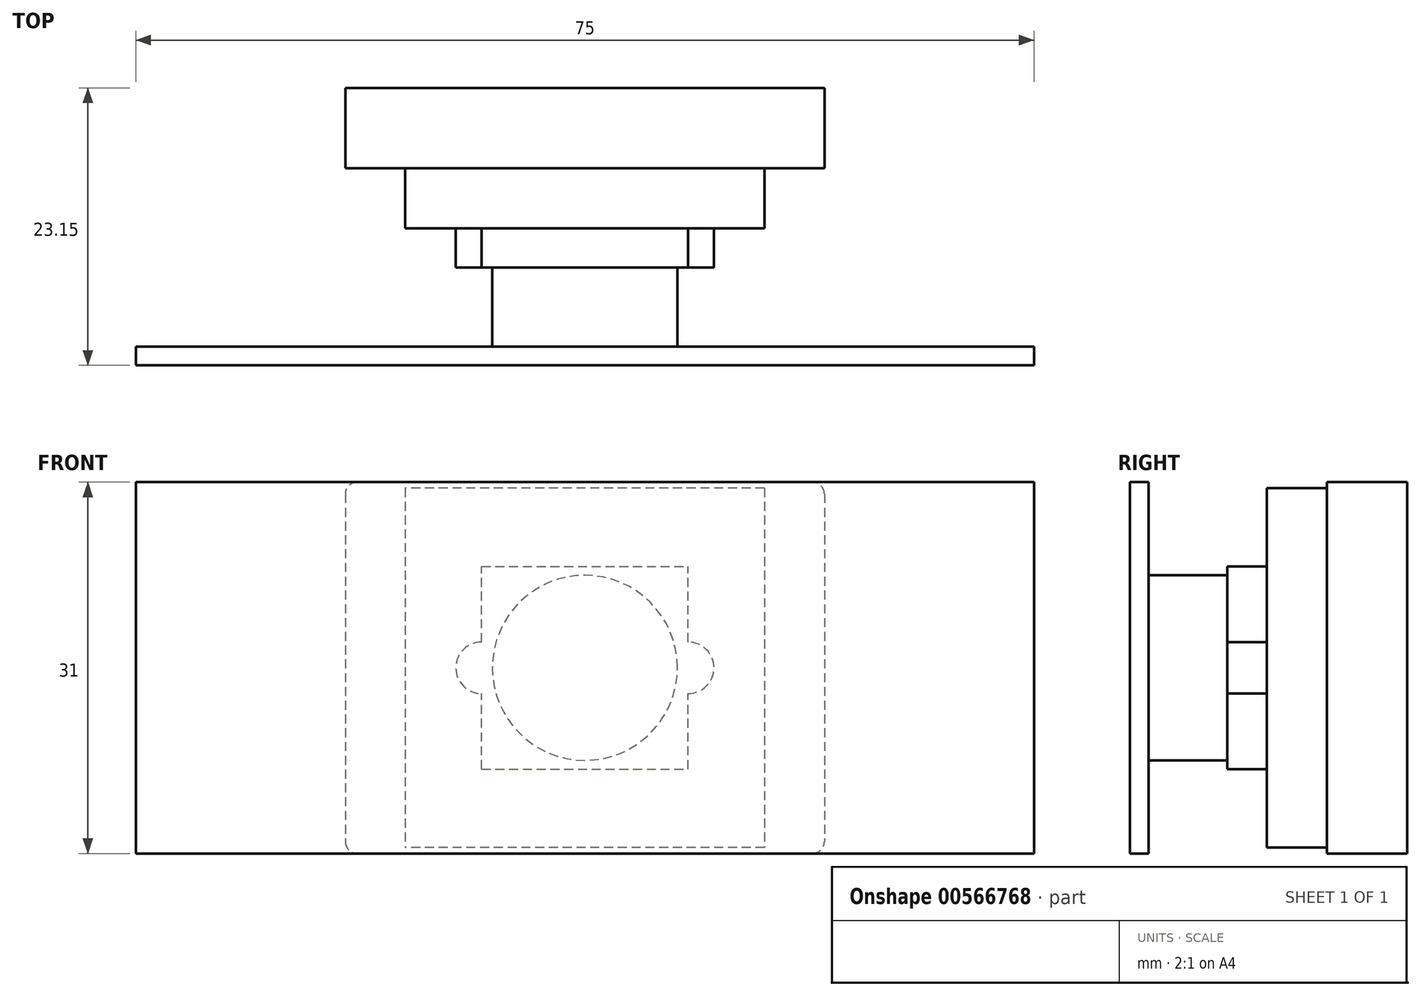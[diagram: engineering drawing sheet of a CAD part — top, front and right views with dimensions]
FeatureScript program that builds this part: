
annotation { "Feature Type Name" : "Feature", "Feature Type Description" : "" }
export const myFeature = defineFeature(function(context is Context, id is Id, definition is map)
    precondition{}
    {
        {
            var Q0;
            Q0=qCreatedBy(makeId("Front.planeOp"),FACE);
            var sketch = newSketch(context, id + "F0", { "sketchPlane" : qUnion([Q0])});
            skLineSegment(sketch, "E0.bottom", {"start": v(20, 15.5) * mm, "end": v(-20, 15.5) * mm});
            skLineSegment(sketch, "E0.top", {"start": v(20, -15.5) * mm, "end": v(-20, -15.5) * mm});
            skLineSegment(sketch, "E0.left", {"start": v(20, 15.5) * mm, "end": v(20, -15.5) * mm});
            skLineSegment(sketch, "E0.right", {"start": v(-20, 15.5) * mm, "end": v(-20, -15.5) * mm});
            skPoint(sketch, "E0.middle", {"position": v(0, 0) * mm});
            skSolve(sketch);
        }
        {
            var Q0;
            Q0=makeQuery(id+"F0.imprint","IMPRINT",FACE,{"disambiguationData":[TD([[makeQuery(id+"F0.imprint","IMPRINT",EDGE,{"derivedFrom":sQuery(id+"F0.wireOp",EDGE,"E0.bottom")}),1.0]])]});
            extrude(context, id + "F1", {"entities" : qUnion([Q0]), "oppositeDirection" : true, "depth" : 6.7 * mm, "offsetDistance" : 25.4 * mm});
        }
        {
            var Q0;
            Q0=makeQuery(id+"F1.opExtrude","SWEPT_EDGE",EDGE,{"disambiguationData":[OSD([sQuery(id+"F0.wireOp",EDGE,"E0.bottom"),sQuery(id+"F0.wireOp",EDGE,"E0.right")])]});
            var Q1;
            Q1=makeQuery(id+"F1.opExtrude","SWEPT_EDGE",EDGE,{"disambiguationData":[OSD([sQuery(id+"F0.wireOp",EDGE,"E0.top"),sQuery(id+"F0.wireOp",EDGE,"E0.right")])]});
            var Q2;
            Q2=makeQuery(id+"F1.opExtrude","SWEPT_EDGE",EDGE,{"disambiguationData":[OSD([sQuery(id+"F0.wireOp",EDGE,"E0.bottom"),sQuery(id+"F0.wireOp",EDGE,"E0.left")])]});
            var Q3;
            Q3=makeQuery(id+"F1.opExtrude","SWEPT_EDGE",EDGE,{"disambiguationData":[OSD([sQuery(id+"F0.wireOp",EDGE,"E0.top"),sQuery(id+"F0.wireOp",EDGE,"E0.left")])]});
            fillet(context, id + "F2", {"entities" : qUnion([Q0, Q1, Q2, Q3]), "radius" : 1 * mm, "tangentPropagation" : true, "allowEdgeOverflow" : false});
        }
        {
            var Q0;
            Q0=makeQuery(id+"F1.opExtrude","CAP_FACE",FACE,{"disambiguationData":[OSD([sQuery(id+"F0.wireOp",EDGE,"E0.bottom"),sQuery(id+"F0.wireOp",EDGE,"E0.top"),sQuery(id+"F0.wireOp",EDGE,"E0.left"),sQuery(id+"F0.wireOp",EDGE,"E0.right")])],"isStart":true});
            var sketch = newSketch(context, id + "F3", { "sketchPlane" : qUnion([Q0])});
            skLineSegment(sketch, "E1.bottom", {"start": v(15, 15) * mm, "end": v(-15, 15) * mm});
            skLineSegment(sketch, "E1.top", {"start": v(15, -15) * mm, "end": v(-15, -15) * mm});
            skLineSegment(sketch, "E1.left", {"start": v(15, 15) * mm, "end": v(15, -15) * mm});
            skLineSegment(sketch, "E1.right", {"start": v(-15, 15) * mm, "end": v(-15, -15) * mm});
            skPoint(sketch, "E1.middle", {"position": v(0, 0) * mm});
            skSolve(sketch);
        }
        {
            var Q0;
            Q0=makeQuery(id+"F3.imprint","IMPRINT",FACE,{"disambiguationData":[TD([[makeQuery(id+"F3.imprint","IMPRINT",EDGE,{"derivedFrom":sQuery(id+"F3.wireOp",EDGE,"E1.bottom")}),1.0]])]});
            extrude(context, id + "F4", {"entities" : qUnion([Q0]), "operationType" : NewBodyOperationType.ADD, "depth" : 5 * mm, "offsetDistance" : 25.4 * mm});
        }
        {
            var Q0;
            Q0=makeQuery(id+"F1.opExtrude","CAP_FACE",FACE,{"disambiguationData":[OSD([sQuery(id+"F0.wireOp",EDGE,"E0.bottom"),sQuery(id+"F0.wireOp",EDGE,"E0.top"),sQuery(id+"F0.wireOp",EDGE,"E0.left"),sQuery(id+"F0.wireOp",EDGE,"E0.right")])],"isStart":true});
            var sketch = newSketch(context, id + "F5", { "sketchPlane" : qUnion([Q0])});
            skLineSegment(sketch, "E2.bottom", {"start": v(8.62, 8.45) * mm, "end": v(-8.62, 8.45) * mm});
            skLineSegment(sketch, "E2.top", {"start": v(8.63, -8.45) * mm, "end": v(-8.62, -8.45) * mm});
            skLineSegment(sketch, "E2.left", {"start": v(8.62, 8.45) * mm, "end": v(8.63, -8.45) * mm});
            skLineSegment(sketch, "E2.right", {"start": v(-8.62, 8.45) * mm, "end": v(-8.62, -8.45) * mm});
            skPoint(sketch, "E2.middle", {"position": v(0, 0) * mm});
            skArc(sketch, "E3", {"start": v(-8.63, 2.15) * mm, "mid": v(-10.78, 0) * mm, "end": v(-8.63, -2.15) * mm});
            skArc(sketch, "E4", {"start": v(8.62, -2.15) * mm, "mid": v(10.78, 0) * mm, "end": v(8.62, 2.15) * mm});
            skSolve(sketch);
        }
        {
            var Q0;
            Q0 = qSketchRegion(id + "F5", true);
            extrude(context, id + "F6", {"entities" : qUnion([Q0]), "operationType" : NewBodyOperationType.ADD, "depth" : 8.3 * mm, "offsetDistance" : 25.4 * mm});
        }
        {
            var Q0;
            Q0=makeQuery(id+"F6.opExtrude","CAP_FACE",FACE,{"disambiguationData":[OSD([sQuery(id+"F5.wireOp",EDGE,"E2.bottom"),sQuery(id+"F5.wireOp",EDGE,"E2.top"),sQuery(id+"F5.wireOp",EDGE,"E2.left"),sQuery(id+"F5.wireOp",EDGE,"E2.right"),sQuery(id+"F5.wireOp",EDGE,"E3"),sQuery(id+"F5.wireOp",EDGE,"E4")])],"isStart":false});
            var sketch = newSketch(context, id + "F7", { "sketchPlane" : qUnion([Q0])});
            skCircle(sketch, "E5", {"center": v(0, 0) * mm, "radius": 7.73 * mm});
            skSolve(sketch);
        }
        {
            var Q0;
            Q0=makeQuery(id+"F7.imprint","IMPRINT",FACE,{"disambiguationData":[TD([[makeQuery(id+"F7.imprint","IMPRINT",EDGE,{"derivedFrom":sQuery(id+"F7.wireOp",EDGE,"E5")}),1.0]])]});
            extrude(context, id + "F8", {"entities" : qUnion([Q0]), "operationType" : NewBodyOperationType.ADD, "depth" : 8.15 * mm, "offsetDistance" : 25.4 * mm});
        }
        {
            var Q0;
            Q0=makeQuery(id+"F8.opExtrude","CAP_FACE",FACE,{"disambiguationData":[OSD([sQuery(id+"F7.wireOp",EDGE,"E5")])],"isStart":false});
            var sketch = newSketch(context, id + "F9", { "sketchPlane" : qUnion([Q0])});
            skLineSegment(sketch, "E6.bottom", {"start": v(37.5, 15.5) * mm, "end": v(-37.5, 15.5) * mm});
            skLineSegment(sketch, "E6.top", {"start": v(37.5, -15.5) * mm, "end": v(-37.5, -15.5) * mm});
            skLineSegment(sketch, "E6.left", {"start": v(37.5, 15.5) * mm, "end": v(37.5, -15.5) * mm});
            skLineSegment(sketch, "E6.right", {"start": v(-37.5, 15.5) * mm, "end": v(-37.5, -15.5) * mm});
            skPoint(sketch, "E6.middle", {"position": v(0, 0) * mm});
            skSolve(sketch);
        }
        {
            var Q0;
            Q0 = qSketchRegion(id + "F9", true);
            extrude(context, id + "F10", {"entities" : qUnion([Q0]), "operationType" : NewBodyOperationType.ADD, "oppositeDirection" : true, "depth" : 1.57 * mm, "offsetDistance" : 25.4 * mm});
        }
    });
